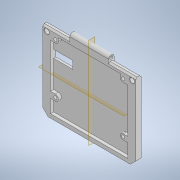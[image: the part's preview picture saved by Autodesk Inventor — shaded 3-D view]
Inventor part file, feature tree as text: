
AUTODESK INVENTOR PART (.ipt)
format: ipt  version: 2022 (Build 260153000, 153)  size: 230,400 bytes
history: native  units: mm
features: sketch x6, extrude x5, chamfer x4, other x3, plane x2, projected_geometry x2, reference x2, fillet x1, hole x1
ambient origin geometry x8: Origin, YZ Plane, XZ Plane, XY Plane, X Axis, Y Axis, Z Axis, Center Point
bodies: Solid1 (feature_tree)
feature tree (26):
  extrude  "Extrusion1"  Depth=50.0mm
  fillet  "Fillet1"  Radius=7.0mm
  extrude  "Extrusion2"  Depth=7.0mm TaperAngle=0.0deg
  plane  "Work Plane1"
  plane  "Work Plane2"
  chamfer  "Chamfer1"  [1 undecoded]
  extrude  "Extrusion3"  Depth=6.0mm TaperAngle=0.0deg
  chamfer  "Chamfer2"  Distance=0.5mm Angle=45.0deg
  extrude  "Extrusion4"  Depth=10.0mm
  hole  "Hole1"  [1 undecoded]
  extrude  "Extrusion5"  Depth=1.0mm
  chamfer  "Chamfer3"  Distance=4.0mm
  chamfer  "Chamfer4"  Distance=87.55mm
  sketch  "Sketch1"  dims[d0=120.0mm d1=50.0mm d2=7.0mm]
  sketch  "Sketch2"  dims[d3=100.0mm d4=7.0mm d5=0.0mm]
  projected_geometry  "Projected Loop1"
  sketch  "Sketch3"  dims[d6=3.5mm]
  reference  "Reference1"
  reference  "Reference2"
  sketch  "Sketch4"  dims[d7=2.0mm d8=0.0mm d9=0.0mm]
  sketch  "Sketch5"  dims[d10=2.0mm d11=2.0mm d12=45.0deg d13=6.0mm d14=0.0mm d15=0.5mm d16=2.0mm d17=45.0deg]
  projected_geometry  "Projected Loop2"
  sketch  "Sketch6"  dims[d18=5.0mm d19=10.0mm d20=10.0mm d21=5.0mm d22=4.0mm d23=0.0mm d24=87.55mm d25=64.9mm d26=4.0mm d27=8.0mm d28=8.0mm d29=8.0mm d30=7.0mm d31=4.0mm d32=6.0mm d33=4.0mm d34=2.0mm d35=90.0deg d36=8.0mm d37=20.594885mm d38=0.0mm d39=0.0mm d40=20.0mm d41=10.0mm d42=25.0mm d43=7.0mm d44=2.0mm d45=45.0deg d46=1.0mm d47=2.0mm d48=45.0deg]
  parser-record x1  (decoder bookkeeping rows leaked as tree rows — omitted from the tree; the rows remain in map.json)
  other  "TFT35 Mount.iam"
  other  "LCD Mount 1:1"
note: 2 required parameter values undecoded (feature->parameter linkage not recoverable at this tier; creation-order binding heuristic only, values carry confidence <= 0.55)
note: 1 file-system path scrubbed to <path> (originals preserved in map.json)
